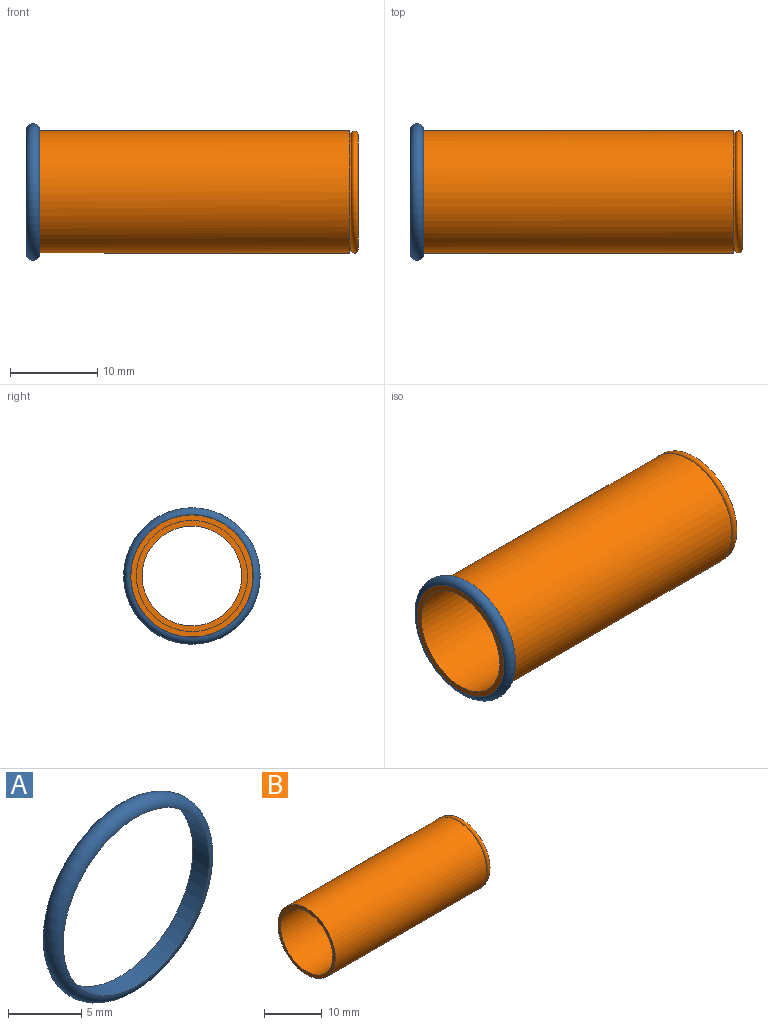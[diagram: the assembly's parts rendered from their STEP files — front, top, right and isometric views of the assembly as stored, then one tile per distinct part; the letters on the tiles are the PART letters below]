
ASSEMBLY  parts=2 mates=1
PART A: 2 faces, bbox 16.9x1.6x16.9 mm
  f0: torus R=7.04mm, axis (0,-1,0), area 118.2mm2, adj f1
  f1: cylinder r=7.04mm len=14.07mm, axis (0,-1,0), area 70.2mm2, adj f0
PART B: 10 faces, bbox 38.1x15.2x15.2 mm
  f0: cylinder r=7.01mm len=37.08mm, axis (-1,0,0), area 1633.2mm2, adj f2,f9
  f1: plane 13.23x13.23mm, normal (1,0,0), area 9.7mm2, adj f7,f8
  f2: plane 14.02x14.02mm, normal (-1,0,0), area 26.7mm2, adj f0,f3
  f3: cylinder r=6.38mm len=34.93mm, axis (-1,0,0), area 1399mm2, adj f2,f4
  f4: plane 12.75x12.75mm, normal (-1,0,0), area 25.1mm2, adj f3,f5
  f5: cylinder r=5.71mm len=11.43mm, axis (-1,0,0), area 28.5mm2, adj f4,f6
  f6: plane 12.75x12.75mm, normal (1,0,0), area 25.1mm2, adj f5,f7
  f7: cylinder r=6.38mm len=12.75mm, axis (-1,0,0), area 95.4mm2, adj f1,f6
  f8: torus R=6.61mm, axis (1,0,0), area 53.8mm2, adj f1,f9
  f9: cone r=6.61mm half-angle=60deg, axis (-1,0,0), area 19.6mm2, adj f0,f8
PLACE A rot(axis=(-0.58,-0.58,-0.58),120deg) t=(-38.1,0,0)mm
PLACE B at identity fixed
MATE fastened A.f0 <-> B.f0  axis (-1,0,0) through (-38.1,0,0)mm
